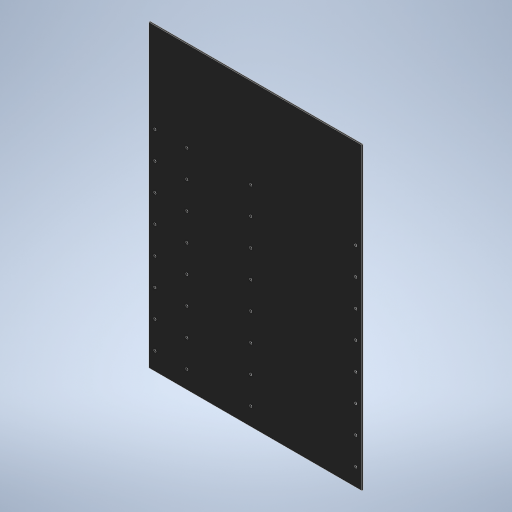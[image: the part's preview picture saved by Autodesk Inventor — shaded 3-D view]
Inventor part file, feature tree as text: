
AUTODESK INVENTOR PART (.ipt)
format: ipt  version: 2024 (Build 280153000, 153)  size: 252,928 bytes
history: native  units: mm
features: sketch x2, other x1, extrude x1, hole x1
ambient origin geometry x8: Origin, YZ Plane, XZ Plane, XY Plane, X Axis, Y Axis, Z Axis, Center Point
bodies: Body1 (feature_tree)
feature tree (5):
  other  "Cladding"
  sketch  "Sketch1"  dims[d0=466.7mm d1=656.0mm]
  extrude  "Extrusion1"  Depth=656.0mm
  hole  "Hole2"  [1 undecoded]
  sketch  "Sketch2"  dims[d2=3.0mm d3=0.0mm d8=440.0mm d9=39.0mm d25=480.0mm d26=70.0mm d27=210.0mm d28=80.0mm d30=60.0mm d31=10.0mm d33=10.0mm d35=5.3mm d36=6.0mm d37=4.0mm d38=2.0mm d39=90.0deg d40=8.0mm d41=20.594885mm d10=0.5mm d11=0.872665mm]
note: 1 required parameter value undecoded (feature->parameter linkage not recoverable at this tier; creation-order binding heuristic only, values carry confidence <= 0.55)
